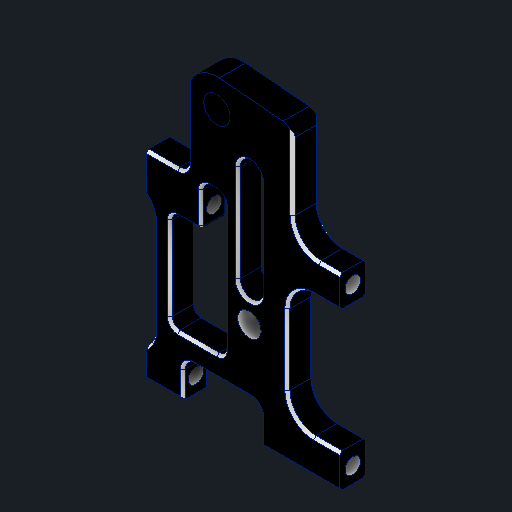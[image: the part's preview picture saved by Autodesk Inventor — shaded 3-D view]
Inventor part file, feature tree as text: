
AUTODESK INVENTOR PART (.ipt)
format: ipt  version: 2024.1 (Build 281209000, 209)  size: 337,920 bytes
history: native  units: mm
features: extrude x4, thread x4, projected_geometry x3, chamfer x2, sketch x1
ambient origin geometry x8: Origin, YZ Plane, XZ Plane, XY Plane, X Axis, Y Axis, Z Axis, Center Point
bodies: Solid1 (feature_tree)
feature tree (14):
  extrude  "Extrusion1"  Depth=0.5mm TaperAngle=45.0deg
  chamfer  "Chamfer1"  Distance=0.5mm Angle=45.0deg
  chamfer  "Chamfer2"  Distance=3.0mm
  extrude  "Extrusion2"  Depth=30.0mm
  extrude  "Extrusion3"  Depth=4.5mm
  thread  "Thread1"  [1 undecoded]
  thread  "Thread2"  [1 undecoded]
  thread  "Thread3"  [1 undecoded]
  thread  "Thread4"  [1 undecoded]
  extrude  "Extrusion4"  Depth=7.0mm TaperAngle=0.0deg
  sketch  "Sketch1"  dims[d0=5.0mm d1=0.0mm d2=0.5mm d3=2.0mm d4=45.0deg d5=0.5mm d6=2.0mm d7=45.0deg d8=3.0mm d9=30.0mm d10=3.0mm d11=3.0mm d12=0.0mm d13=10.0mm d14=0.0mm d15=10.5mm d16=0.0mm d17=7.0mm d18=0.0mm d19=15.0mm d20=0.0mm d21=15.0mm d22=0.0mm d23=4.5mm d24=0.0mm d25=0.0mm]
  projected_geometry  "Projected Loop1"
  projected_geometry  "Projected Loop2"
  projected_geometry  "Projected Loop3"
note: 4 required parameter values undecoded (feature->parameter linkage not recoverable at this tier; creation-order binding heuristic only, values carry confidence <= 0.55)
